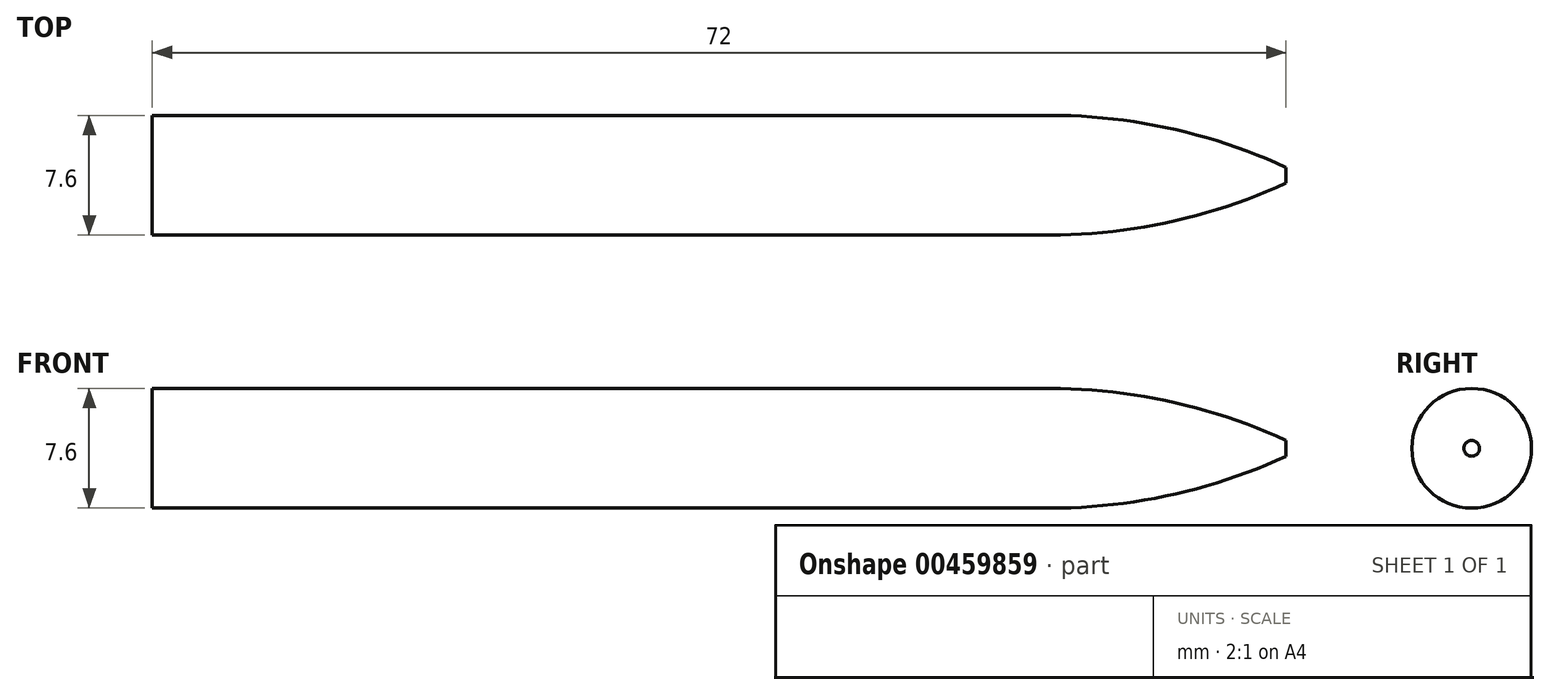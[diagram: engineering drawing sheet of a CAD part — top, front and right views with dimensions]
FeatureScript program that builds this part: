
annotation { "Feature Type Name" : "Feature", "Feature Type Description" : "" }
export const myFeature = defineFeature(function(context is Context, id is Id, definition is map)
    precondition{}
    {
        {
            var Q0;
            Q0=qCreatedBy(makeId("Front.planeOp"),FACE);
            var sketch = newSketch(context, id + "F0", { "sketchPlane" : qUnion([Q0])});
            skLineSegment(sketch, "E0", {"start": v(0, 0) * mm, "end": v(72, 0) * mm});
            skLineSegment(sketch, "E1", {"start": v(0, 0) * mm, "end": v(0, 3.8) * mm});
            skLineSegment(sketch, "E2", {"start": v(0, 3.8) * mm, "end": v(57, 3.8) * mm});
            skLineSegment(sketch, "E3", {"start": v(72, 0) * mm, "end": v(72, 0.5) * mm});
            skArc(sketch, "E4", {"start": v(57, 3.8) * mm, "mid": v(64.68, 2.97) * mm, "end": v(72, 0.5) * mm});
            skSolve(sketch);
        }
        {
            var Q0;
            Q0=makeQuery(id+"F0.imprint","IMPRINT",FACE,{"disambiguationData":[TD([[makeQuery(id+"F0.imprint","IMPRINT",EDGE,{"derivedFrom":sQuery(id+"F0.wireOp",EDGE,"E0")}),1.0]])]});
            var Q1;
            Q1=sQuery(id+"F0.wireOp",EDGE,"E0");
            revolve(context, id + "F1", {"entities" : qUnion([Q0]), "axis" : qUnion([Q1]), "revolveType" : RevolveType.FULL});
        }
    });
